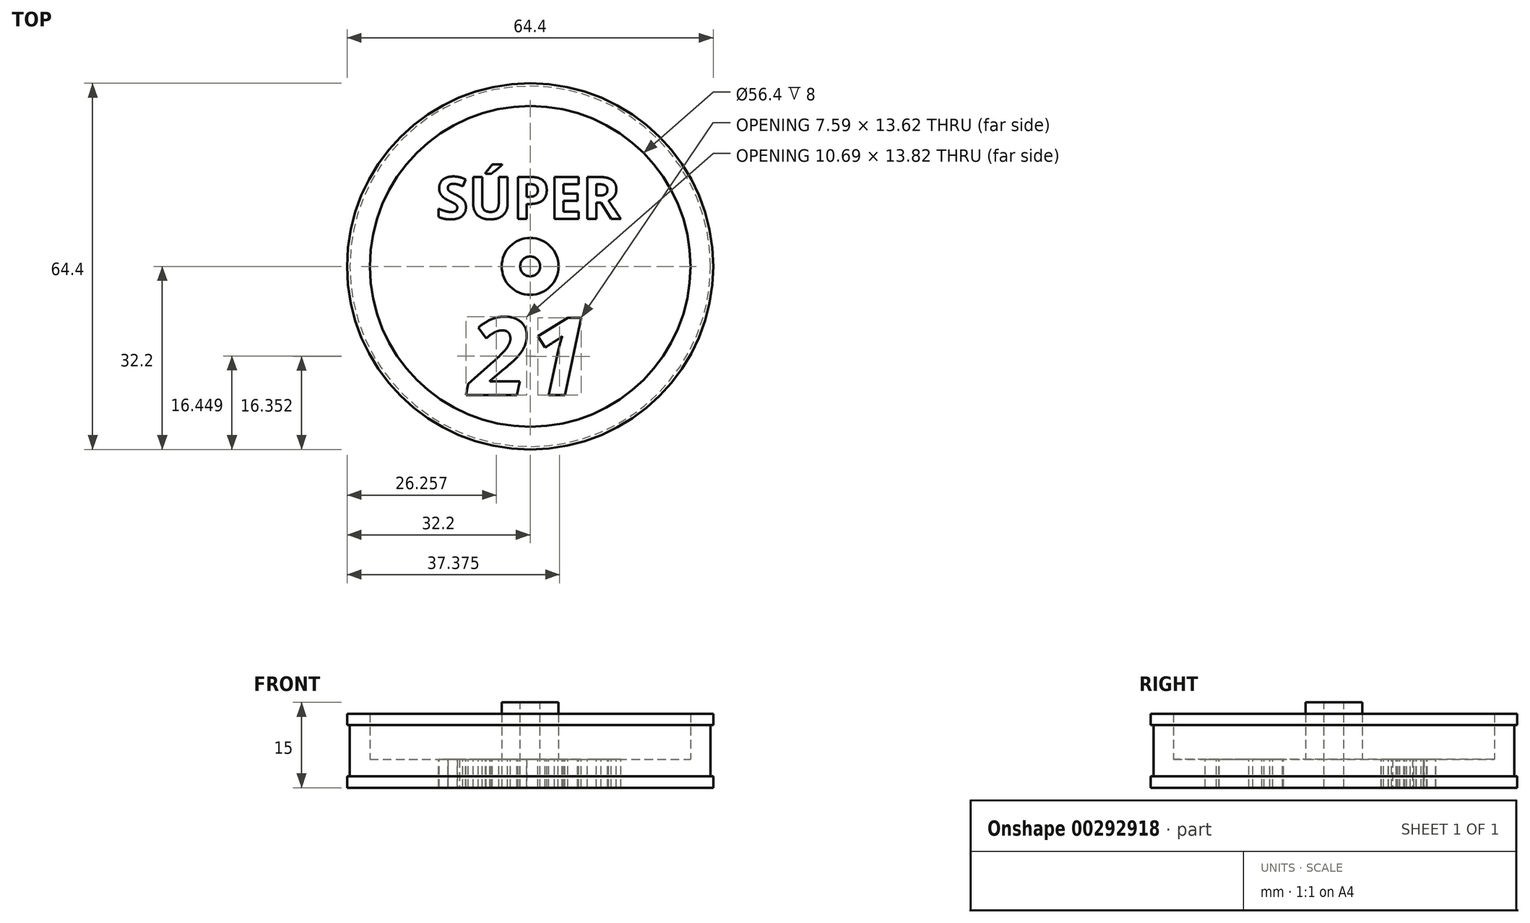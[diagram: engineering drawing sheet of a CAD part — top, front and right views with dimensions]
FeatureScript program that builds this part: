
annotation { "Feature Type Name" : "Feature", "Feature Type Description" : "" }
export const myFeature = defineFeature(function(context is Context, id is Id, definition is map)
    precondition{}
    {
        {
            var Q0;
            Q0=qCreatedBy(makeId("Front.planeOp"),FACE);
            var sketch = newSketch(context, id + "F0", { "sketchPlane" : qUnion([Q0])});
            skLineSegment(sketch, "E0", {"start": v(0, 0) * mm, "end": v(32.2, 0) * mm});
            skLineSegment(sketch, "E1", {"start": v(32.2, 0) * mm, "end": v(32.2, 2) * mm});
            skLineSegment(sketch, "E2", {"start": v(32.2, 2) * mm, "end": v(31.7, 2) * mm});
            skLineSegment(sketch, "E3", {"start": v(31.7, 2) * mm, "end": v(31.7, 11) * mm});
            skLineSegment(sketch, "E4", {"start": v(31.7, 11) * mm, "end": v(32.2, 11) * mm});
            skLineSegment(sketch, "E5", {"start": v(32.2, 11) * mm, "end": v(32.2, 13) * mm});
            skLineSegment(sketch, "E6", {"start": v(32.2, 13) * mm, "end": v(28.2, 13) * mm});
            skLineSegment(sketch, "E7", {"start": v(28.2, 13) * mm, "end": v(28.2, 5) * mm});
            skLineSegment(sketch, "E8", {"start": v(28.2, 5) * mm, "end": v(0, 5) * mm});
            skLineSegment(sketch, "E9", {"start": v(0, 0) * mm, "end": v(0, 5) * mm});
            skSolve(sketch);
        }
        {
            var Q0;
            Q0=makeQuery(id+"F0.imprint","IMPRINT",FACE,{"disambiguationData":[TD([[makeQuery(id+"F0.imprint","IMPRINT",EDGE,{"derivedFrom":sQuery(id+"F0.wireOp",EDGE,"E0")}),1.0]])]});
            var Q1;
            Q1=sQuery(id+"F0.wireOp",EDGE,"E9");
            revolve(context, id + "F1", {"entities" : qUnion([Q0]), "axis" : qUnion([Q1]), "revolveType" : RevolveType.FULL});
        }
        {
            var Q0;
            Q0=makeQuery(id+"F1.opRevolve","SWEPT_FACE",FACE,{"disambiguationData":[OSD([sQuery(id+"F0.wireOp",EDGE,"E8")])]});
            var sketch = newSketch(context, id + "F2", { "sketchPlane" : qUnion([Q0])});
            skCircle(sketch, "E10.0", {"center": v(0, 0) * mm, "radius": 28.2 * mm});
            skCircle(sketch, "E11", {"center": v(0, 0) * mm, "radius": 5 * mm});
            skSolve(sketch);
        }
        {
            var Q0;
            Q0=makeQuery(id+"F2.imprint","IMPRINT",FACE,{"disambiguationData":[TD([[makeQuery(id+"F2.imprint","IMPRINT",EDGE,{"derivedFrom":sQuery(id+"F2.wireOp",EDGE,"E11")}),1.0]])]});
            extrude(context, id + "F3", {"entities" : qUnion([Q0]), "operationType" : NewBodyOperationType.ADD, "depth" : 10 * mm});
        }
        {
            var Q0;
            Q0=makeQuery(id+"F3.opExtrude","CAP_FACE",FACE,{"disambiguationData":[OSD([sQuery(id+"F2.wireOp",EDGE,"E11")])],"isStart":false});
            var sketch = newSketch(context, id + "F4", { "sketchPlane" : qUnion([Q0])});
            skCircle(sketch, "E12.0", {"center": v(0, 0) * mm, "radius": 5 * mm});
            skCircle(sketch, "E13", {"center": v(0, 0) * mm, "radius": 1.75 * mm});
            skSolve(sketch);
        }
        {
            var Q0;
            Q0=makeQuery(id+"F4.imprint","IMPRINT",FACE,{"disambiguationData":[TD([[makeQuery(id+"F4.imprint","IMPRINT",EDGE,{"derivedFrom":sQuery(id+"F4.wireOp",EDGE,"E13")}),1.0]])]});
            extrude(context, id + "F5", {"entities" : qUnion([Q0]), "operationType" : NewBodyOperationType.REMOVE, "oppositeDirection" : true, "depth" : 25 * mm});
        }
        {
            var Q0;
            Q0=makeQuery(id+"F1.opRevolve","SWEPT_FACE",FACE,{"disambiguationData":[OSD([sQuery(id+"F0.wireOp",EDGE,"E8")])]});
            var sketch = newSketch(context, id + "F6", { "sketchPlane" : qUnion([Q0])});
            skText(sketch, "E14", { "text": "SÚPER", "fontName": "OpenSans-Bold.ttf"});
            skText(sketch, "E15", { "text": "21", "fontName": "OpenSans-BoldItalic.ttf"});
            const initialGuessF6  = {"E14": [-0.01656, 0.00836, 1, 0, 0.00742], "E15": [-0.01083, -0.02266, 1, 0, 0.01374]};
            skSetInitialGuess(sketch, initialGuessF6);
            skSolve(sketch);
        }
        {
            var Q0;
            Q0 = qSketchRegion(id + "F6", true);
            extrude(context, id + "F7", {"entities" : qUnion([Q0]), "operationType" : NewBodyOperationType.REMOVE, "oppositeDirection" : true, "depth" : 25 * mm});
        }
    });
